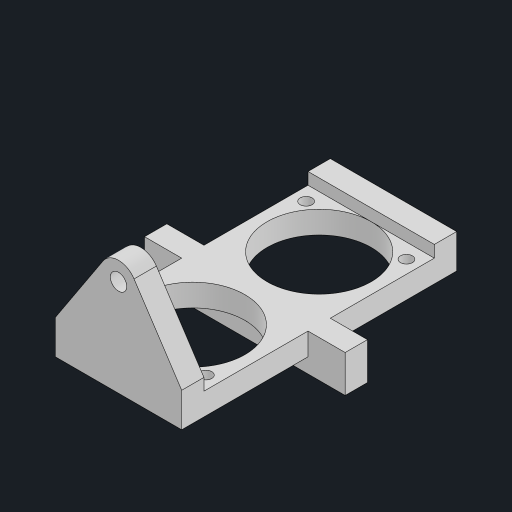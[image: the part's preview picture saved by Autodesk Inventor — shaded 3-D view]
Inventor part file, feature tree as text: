
AUTODESK INVENTOR PART (.ipt)
format: ipt  version: 2023 (Build 270158000, 158)  size: 181,248 bytes
history: native  units: mm
features: sketch x4, extrude x4, other x1, hole x1
ambient origin geometry x8: Origin, YZ Plane, XZ Plane, XY Plane, X Axis, Y Axis, Z Axis, Center Point
bodies: Body1 (feature_tree)
feature tree (10):
  other  "ソリッド1"
  sketch  "スケッチ1"
  extrude  "押し出し1"  Depth=3.0mm
  extrude  "押し出し2"  Depth=3.0mm TaperAngle=0.0deg
  extrude  "押し出し4"  Depth=1.6mm TaperAngle=0.0deg
  extrude  "押し出し3"  Depth=10.0mm
  hole  "穴1"  [1 undecoded]
  sketch  "スケッチ2"
  sketch  "スケッチ3"
  sketch  "スケッチ4"
note: 1 required parameter value undecoded (feature->parameter linkage not recoverable at this tier; creation-order binding heuristic only, values carry confidence <= 0.55)
